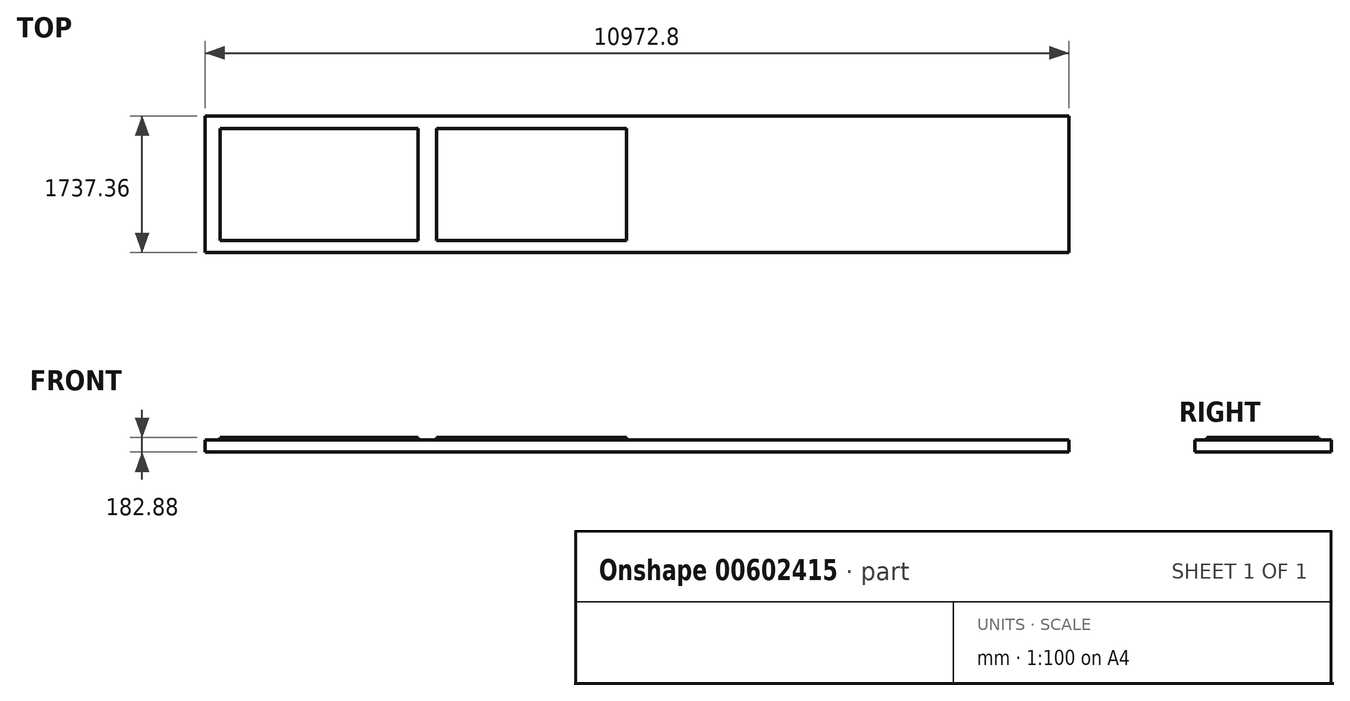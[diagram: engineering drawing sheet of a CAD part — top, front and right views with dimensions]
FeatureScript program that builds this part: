
annotation { "Feature Type Name" : "Feature", "Feature Type Description" : "" }
export const myFeature = defineFeature(function(context is Context, id is Id, definition is map)
    precondition{}
    {
        {
            var Q0;
            Q0=qCreatedBy(makeId("Top.planeOp"),FACE);
            var sketch = newSketch(context, id + "F0", { "sketchPlane" : qUnion([Q0])});
            skLineSegment(sketch, "E0.bottom", {"start": v(0, 0) * mm, "end": v(10972.8, 0) * mm});
            skLineSegment(sketch, "E0.top", {"start": v(0, -1737.36) * mm, "end": v(10972.8, -1737.36) * mm});
            skLineSegment(sketch, "E0.left", {"start": v(0, 0) * mm, "end": v(0, -1737.36) * mm});
            skLineSegment(sketch, "E0.right", {"start": v(10972.8, 0) * mm, "end": v(10972.8, -1737.36) * mm});
            skSolve(sketch);
        }
        {
            var Q0;
            Q0=makeQuery(id+"F0.imprint","IMPRINT",FACE,{"disambiguationData":[TD([[makeQuery(id+"F0.imprint","IMPRINT",EDGE,{"derivedFrom":sQuery(id+"F0.wireOp",EDGE,"E0.bottom")}),-1.0]])]});
            extrude(context, id + "F1", {"entities" : qUnion([Q0]), "depth" : 152.4 * mm, "offsetDistance" : 30.48 * mm});
        }
        {
            var Q0;
            Q0=makeQuery(id+"F1.opExtrude","CAP_FACE",FACE,{"disambiguationData":[OSD([sQuery(id+"F0.wireOp",EDGE,"E0.bottom"),sQuery(id+"F0.wireOp",EDGE,"E0.top"),sQuery(id+"F0.wireOp",EDGE,"E0.left"),sQuery(id+"F0.wireOp",EDGE,"E0.right")])],"isStart":false});
            var sketch = newSketch(context, id + "F2", { "sketchPlane" : qUnion([Q0])});
            skLineSegment(sketch, "E1.bottom", {"start": v(193.3, -162.2) * mm, "end": v(2707.37, -162.2) * mm});
            skLineSegment(sketch, "E1.top", {"start": v(193.3, -1584.8) * mm, "end": v(2707.37, -1584.8) * mm});
            skLineSegment(sketch, "E1.left", {"start": v(193.3, -162.2) * mm, "end": v(193.3, -1584.8) * mm});
            skLineSegment(sketch, "E1.right", {"start": v(2707.37, -162.2) * mm, "end": v(2707.37, -1584.8) * mm});
            skLineSegment(sketch, "E2.bottom", {"start": v(2940.38, -162.2) * mm, "end": v(5356.32, -162.2) * mm});
            skLineSegment(sketch, "E2.top", {"start": v(2940.38, -1584.8) * mm, "end": v(5356.32, -1584.8) * mm});
            skLineSegment(sketch, "E2.left", {"start": v(2940.38, -162.2) * mm, "end": v(2940.38, -1584.8) * mm});
            skLineSegment(sketch, "E2.right", {"start": v(5356.32, -162.2) * mm, "end": v(5356.32, -1584.8) * mm});
            skSolve(sketch);
        }
        {
            var Q0;
            Q0=makeQuery(id+"F2.imprint","IMPRINT",FACE,{"disambiguationData":[TD([[makeQuery(id+"F2.imprint","IMPRINT",EDGE,{"derivedFrom":sQuery(id+"F2.wireOp",EDGE,"E1.bottom")}),-1.0]])]});
            var Q1;
            Q1=makeQuery(id+"F2.imprint","IMPRINT",FACE,{"disambiguationData":[TD([[makeQuery(id+"F2.imprint","IMPRINT",EDGE,{"derivedFrom":sQuery(id+"F2.wireOp",EDGE,"E2.bottom")}),-1.0]])]});
            extrude(context, id + "F3", {"entities" : qUnion([Q0, Q1]), "operationType" : NewBodyOperationType.ADD, "depth" : 30.48 * mm, "offsetDistance" : 30.48 * mm});
        }
    });
